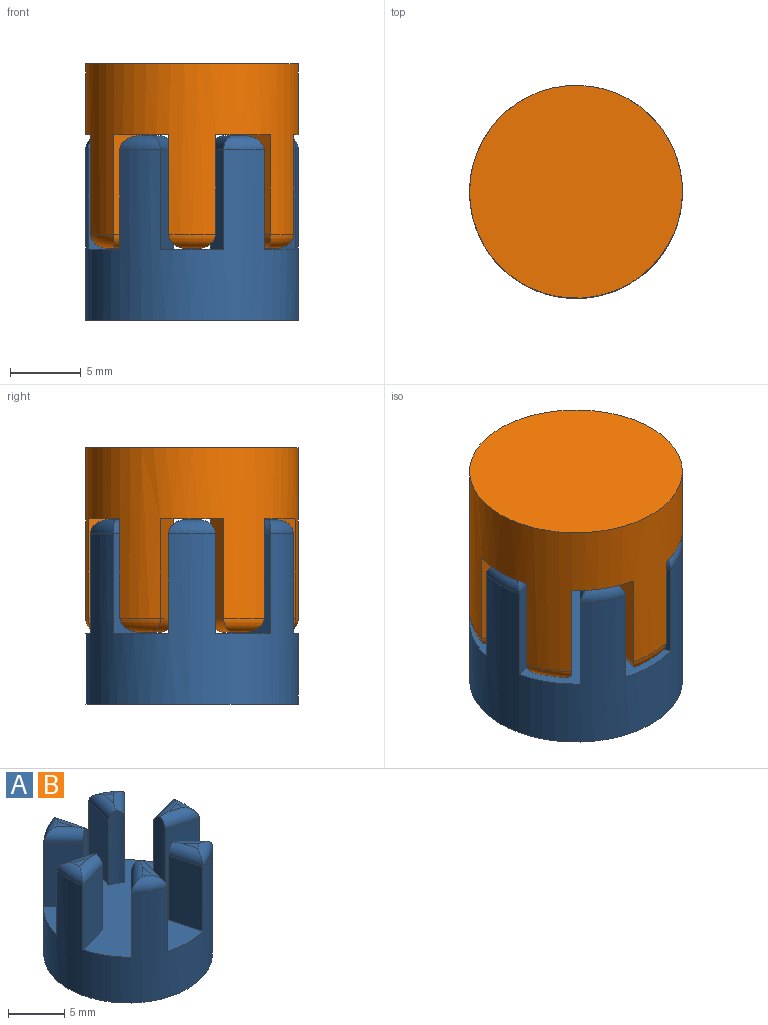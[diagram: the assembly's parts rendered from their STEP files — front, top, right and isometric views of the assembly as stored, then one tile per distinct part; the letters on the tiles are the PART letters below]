
ASSEMBLY  parts=2 mates=1
PART A: 45 faces, bbox 16.2x15.5x13 mm
  f0: cylinder r=4mm len=7.96mm, axis (0,0,-1), area 11.5mm2, adj f13,f25,f26,f43,f44
  f1: plane 1.47x1.07mm, normal (0,0,1), area 0.6mm2, adj f42,f43,f44
  f2: cylinder r=4mm len=7.96mm, axis (0,0,-1), area 11.5mm2, adj f13,f23,f24,f28,f29
  f3: plane 1.47x1.07mm, normal (0,0,1), area 0.6mm2, adj f27,f28,f29
  f4: cylinder r=4mm len=7.96mm, axis (0,0,-1), area 11.5mm2, adj f13,f21,f22,f40,f41
  f5: plane 1.48x0.79mm, normal (0,0,1), area 0.6mm2, adj f39,f40,f41
  f6: cylinder r=4mm len=7.96mm, axis (0,0,-1), area 11.5mm2, adj f13,f19,f20,f37,f38
  f7: plane 1.47x1.07mm, normal (0,0,1), area 0.6mm2, adj f36,f37,f38
  f8: cylinder r=4mm len=7.96mm, axis (0,0,-1), area 11.5mm2, adj f13,f17,f18,f34,f35
  f9: plane 1.47x1.07mm, normal (0,0,1), area 0.6mm2, adj f33,f34,f35
  f10: cylinder r=4mm len=7.96mm, axis (0,0,-1), area 11.5mm2, adj f13,f15,f16,f31,f32
  f11: plane 1.48x0.79mm, normal (0,0,1), area 0.6mm2, adj f30,f31,f32
  f12: cylinder r=7.5mm len=15mm, axis (0,0,-1), area 375.3mm2, adj f13,f14,f15,f16,f17,f18,f19,f20
  f13: plane 15x14.63mm, normal (0,0,1), area 126.1mm2, adj f0,f2,f4,f6,f8,f10,f12,f15
  f14: plane 15x15mm, normal (0,0,-1), area 176.7mm2, adj f12
  f15: plane 7x3.39mm, normal (-0.26,-0.97,0), area 24.5mm2, adj f10,f12,f13,f32
  f16: plane 7x3.39mm, normal (-0.26,0.97,0), area 24.5mm2, adj f10,f12,f13,f31
  f17: plane 7x3.39mm, normal (-0.97,-0.26,0), area 24.5mm2, adj f8,f12,f13,f35
  f18: plane 7x2.48mm, normal (0.71,0.71,0), area 24.5mm2, adj f8,f12,f13,f34
  f19: plane 7x3.39mm, normal (0.97,-0.26,0), area 24.5mm2, adj f6,f12,f13,f37
  f20: plane 7x2.48mm, normal (-0.71,0.71,0), area 24.5mm2, adj f6,f12,f13,f38
  f21: plane 7x3.39mm, normal (0.26,0.97,0), area 24.5mm2, adj f4,f12,f13,f41
  f22: plane 7x3.39mm, normal (0.26,-0.97,0), area 24.5mm2, adj f4,f12,f13,f40
  f23: plane 7x2.48mm, normal (-0.71,-0.71,0), area 24.5mm2, adj f2,f12,f13,f28
  f24: plane 7x3.39mm, normal (0.97,0.26,0), area 24.5mm2, adj f2,f12,f13,f29
  f25: plane 7x3.39mm, normal (-0.97,0.26,0), area 24.5mm2, adj f0,f12,f13,f43
  f26: plane 7x2.48mm, normal (0.71,-0.71,0), area 24.5mm2, adj f0,f12,f13,f44
  f27: torus R=6.5mm, axis (0,0,1), area 3.8mm2, adj f3,f12,f28,f29
  f28: cylinder r=1mm len=3.27mm, axis (0.71,-0.71,0), area 4.8mm2, adj f2,f3,f23,f27,f29
  f29: cylinder r=1mm len=3.77mm, axis (-0.26,0.97,0), area 4.8mm2, adj f2,f3,f24,f27,f28
  f30: torus R=6.5mm, axis (0,0,1), area 3.8mm2, adj f11,f12,f31,f32
  f31: cylinder r=1mm len=3.77mm, axis (-0.97,-0.26,0), area 4.8mm2, adj f10,f11,f16,f30,f32
  f32: cylinder r=1mm len=3.77mm, axis (0.97,-0.26,0), area 4.8mm2, adj f10,f11,f15,f30,f31
  f33: torus R=6.5mm, axis (0,0,1), area 3.8mm2, adj f9,f12,f34,f35
  f34: cylinder r=1mm len=3.27mm, axis (-0.71,0.71,0), area 4.8mm2, adj f8,f9,f18,f33,f35
  f35: cylinder r=1mm len=3.77mm, axis (0.26,-0.97,0), area 4.8mm2, adj f8,f9,f17,f33,f34
  f36: torus R=6.5mm, axis (0,0,1), area 3.8mm2, adj f7,f12,f37,f38
  f37: cylinder r=1mm len=3.77mm, axis (0.26,0.97,0), area 4.8mm2, adj f6,f7,f19,f36,f38
  f38: cylinder r=1mm len=3.27mm, axis (-0.71,-0.71,0), area 4.8mm2, adj f6,f7,f20,f36,f37
  f39: torus R=6.5mm, axis (0,0,1), area 3.8mm2, adj f5,f12,f40,f41
  f40: cylinder r=1mm len=3.77mm, axis (0.97,0.26,0), area 4.8mm2, adj f4,f5,f22,f39,f41
  f41: cylinder r=1mm len=3.77mm, axis (-0.97,0.26,0), area 4.8mm2, adj f4,f5,f21,f39,f40
  f42: torus R=6.5mm, axis (0,0,1), area 3.8mm2, adj f1,f12,f43,f44
  f43: cylinder r=1mm len=3.77mm, axis (-0.26,-0.97,0), area 4.8mm2, adj f0,f1,f25,f42,f44
  f44: cylinder r=1mm len=3.27mm, axis (0.71,0.71,0), area 4.8mm2, adj f0,f1,f26,f42,f43
PART B: same geometry as A
PLACE A at identity fixed
PLACE B rot(axis=(0.97,-0.26,0),180deg) t=(0,0,8.06)mm
MATE cylindrical B.f12 <-> A.f12  axis (0,0,1) through (0,0,7.06)mm
